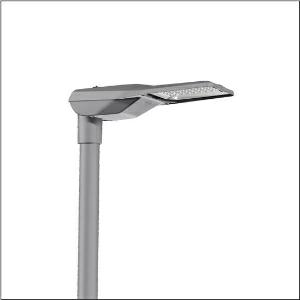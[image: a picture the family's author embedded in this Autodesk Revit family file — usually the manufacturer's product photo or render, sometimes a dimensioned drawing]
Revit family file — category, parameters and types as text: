
# Revit family: streetlight_sl_21_iq_mini___st1_0a_5xe2d31v08gb_747e
name_source: partatom
category: Lighting Fixtures
units: mm (PartAtom-declared; Revit-internal decimal feet)

## family parameters
Cut with Voids When Loaded = No
Host = Face
Light Source = No
Part Type = Normal
Room Calculation Point = No
Round Connector Dimension = Use Diameter
Shared = No

## types (1)
- --- (1 x LED, 5990 lm, 39.8 W, 3000K)
    Apparent Load = 40 VA
    CIE Flux Codes = 37 72 97 100 100
    Color Rendering = 70
    Color Temperature = 3000K
    Default Elevation = 1800 mm
    Description = Streetlight SL 21 iQ mini, mast luminaire, primary light control with lens, of PMMA, primary optical cover: cover, of toughened safety glass, transparent, light distribution: ST1.0a, light emission: direct distribution, primary light characteristic: asymmetric, installation type: post-top, side-entry, LED, High Power LED, rated luminous flux: 5.990lm, luminous efficacy: 151lm/W, light colour: 730, colour temperature: 3000K, control: presetting dimming logarithmic, Street-Remote, Auto-Match, Temp-Guard, Lumen-Switch, Night-Set, Smart-Wire, Light-Fading, Desk-Remote (wireless, voltage-free reading and setting of iQ features in the workshop via application-optimized NFC function/RFID function), optimised constant luminous flux control (CLO 2.0), mains connection: 220..240V, AC, 50/60Hz, start of lifetime: 40W, end of service life: 41W, reduction: 18W, luminaire housing, of diecast aluminium, powder-coated, Siteco® metallic grey (DB 702S), corrosivity category C5 mid according to DIN EN ISO 12944, please order mast flange separately, inclination adjustable: 0°, 5°, 10°, 15°, sealing non-destructively replaceable, multi-level sealing system, length: 628mm, width: 235mm, height: 110mm, mast flange for spigot size: 42mm (side-entry): 5XC10008XM4, 60/48mm (side-entry/post-top): 5XC10108XM2, 76/60mm (side-entry/post-top): 5XC10108XM1, Smart Interface above, protection rating (complete): IP66, insulation class (complete): insulation class II (safety insulation), certification: CE, ENEC, ENEC+, VDE, impact resistance: IK09, permissible operating ambient temperature for outdoor applications: -40..+50°C, standard-compliant lighting for roads and squares, packaging unit: 1 piece

Light Distribution: ST1.0a
    Height = 110 mm
    Lamp = 1 x LED
    Lamp Light Flux = 5990 lm
    Lamp Power = 39.8 W
    Lamp count = 1
    Length = 625 mm
    Luminous efficacy = 151 lm/W
    Manufacturer = Siteco
    ModVariant = No
    Model = 5XE2D31V08GB
    Number of Poles = 1
    OnlyDefault = Yes
    Power Factor = 1
    Product Name = Streetlight SL 21 iQ mini | ST1.0a
    Product group = mast luminaire | pylon top
    ProductGroupID = 6100
    Protection Class = Protection class II
    Protection Degree = IP 66
    RLX_Detail_Level = 1
    RLX_Emergency_Light_Flux = 0 lm
    RLX_Emergency_Type = 0
    RLX_Emergency_Type_DB = No
    RlxData = <blob elided: 92873 chars, md5=abcb8388>
    Socket = socket
    Standby Power = 0 W
    System Light Flux = 5990 lm
    System Power = 40 W
    Type Comments = factory setting: luminous flux: 100 % | dim-lin: 254 | 800 mA
    Type Image = l_1003515.jpg
    URL = http://relux.com
    VarID = @adj_045187
    Voltage = 0 V
    Weight = 0.00 kg
    Width = 234 mm

## geometry (parser evidence)
native form markers: Blend x4, Sweep x12
no freeform markers — native parametric forms only
